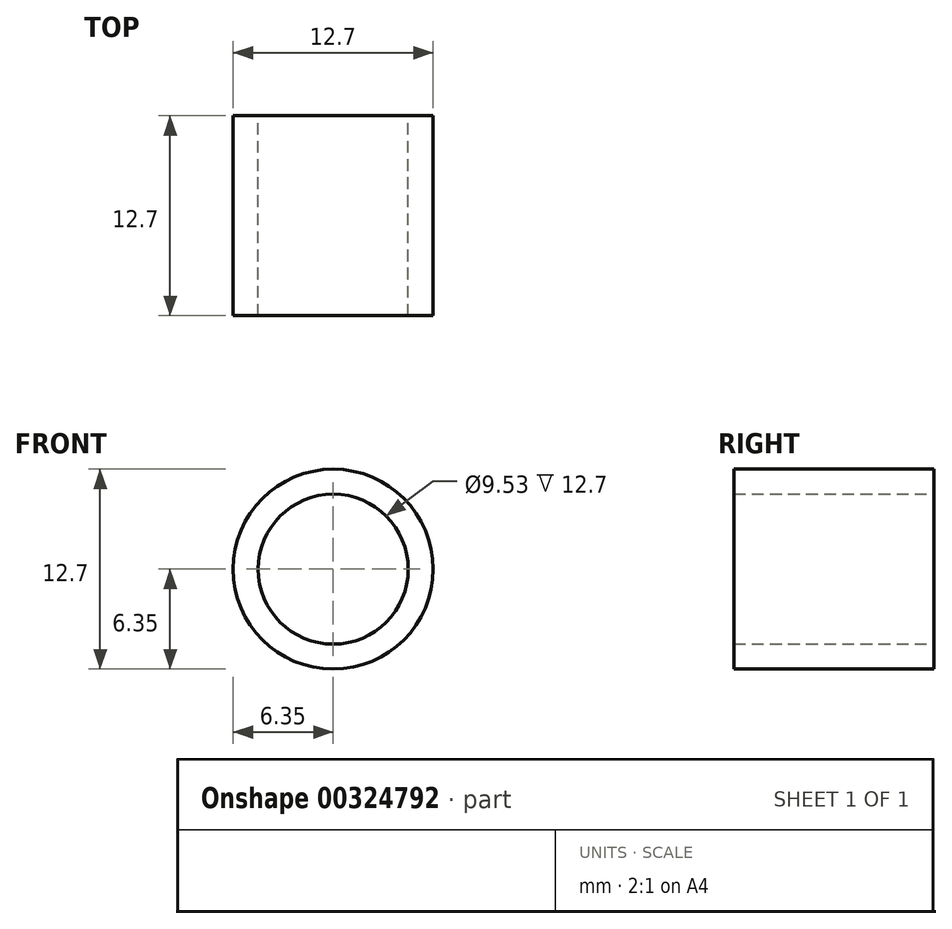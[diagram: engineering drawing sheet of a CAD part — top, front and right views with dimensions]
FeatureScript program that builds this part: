
annotation { "Feature Type Name" : "Feature", "Feature Type Description" : "" }
export const myFeature = defineFeature(function(context is Context, id is Id, definition is map)
    precondition{}
    {
        {
            var Q0;
            Q0=qCreatedBy(makeId("Front.planeOp"),FACE);
            var sketch = newSketch(context, id + "F0", { "sketchPlane" : qUnion([Q0])});
            skCircle(sketch, "E0", {"center": v(0, 0) * mm, "radius": 4.76 * mm});
            skCircle(sketch, "E1", {"center": v(0, 0) * mm, "radius": 6.35 * mm});
            skSolve(sketch);
        }
        {
            var Q0;
            Q0=makeQuery(id+"F0.imprint","IMPRINT",FACE,{"disambiguationData":[TD([[makeQuery(id+"F0.imprint","IMPRINT",EDGE,{"derivedFrom":sQuery(id+"F0.wireOp",EDGE,"E0")}),-1.0]])]});
            extrude(context, id + "F1", {"entities" : qUnion([Q0]), "depth" : 12.7 * mm, "offsetDistance" : 25.4 * mm});
        }
    });
